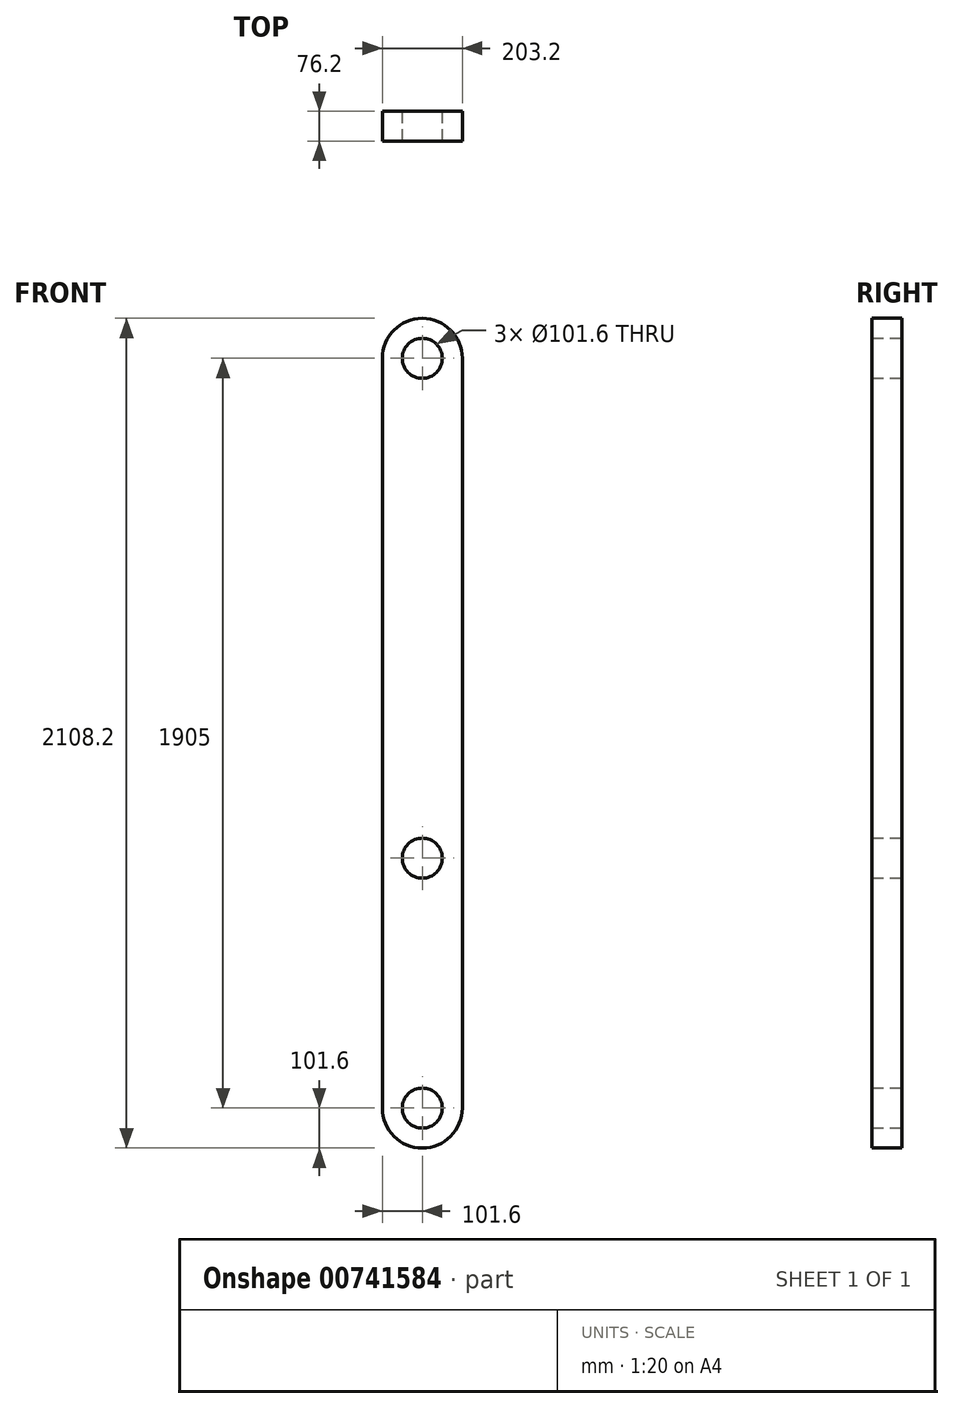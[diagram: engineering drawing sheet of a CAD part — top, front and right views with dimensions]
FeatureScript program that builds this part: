
annotation { "Feature Type Name" : "Feature", "Feature Type Description" : "" }
export const myFeature = defineFeature(function(context is Context, id is Id, definition is map)
    precondition{}
    {
        {
            var Q0;
            Q0=qCreatedBy(makeId("Front.planeOp"),FACE);
            var sketch = newSketch(context, id + "F0", { "sketchPlane" : qUnion([Q0])});
            skLineSegment(sketch, "E0.bottom", {"start": v(101.6, 0) * mm, "end": v(101.6, 0) * mm});
            skLineSegment(sketch, "E0.top", {"start": v(101.6, 2108.2) * mm, "end": v(101.6, 2108.2) * mm});
            skLineSegment(sketch, "E0.left", {"start": v(0, 101.6) * mm, "end": v(0, 2006.6) * mm});
            skLineSegment(sketch, "E0.right", {"start": v(203.2, 101.6) * mm, "end": v(203.2, 2006.6) * mm});
            skPoint(sketch, "E1.visualSharp", {"position": v(0, 2108.2) * mm});
            skArc(sketch, "E1.filletArc", {"start": v(101.6, 2108.2) * mm, "mid": v(29.76, 2078.44) * mm, "end": v(0, 2006.6) * mm});
            skPoint(sketch, "E2.visualSharp", {"position": v(0, 0) * mm});
            skArc(sketch, "E2.filletArc", {"start": v(0, 101.6) * mm, "mid": v(29.76, 29.76) * mm, "end": v(101.6, 0) * mm});
            skPoint(sketch, "E3.visualSharp", {"position": v(203.2, 0) * mm});
            skArc(sketch, "E3.filletArc", {"start": v(101.6, 0) * mm, "mid": v(173.44, 29.76) * mm, "end": v(203.2, 101.6) * mm});
            skPoint(sketch, "E4.visualSharp", {"position": v(203.2, 2108.2) * mm});
            skArc(sketch, "E4.filletArc", {"start": v(203.2, 2006.6) * mm, "mid": v(173.44, 2078.44) * mm, "end": v(101.6, 2108.2) * mm});
            skCircle(sketch, "E5", {"center": v(101.6, 2006.6) * mm, "radius": 50.8 * mm});
            skCircle(sketch, "E6", {"center": v(101.6, 101.6) * mm, "radius": 50.8 * mm});
            skCircle(sketch, "E7", {"center": v(101.6, 736.6) * mm, "radius": 50.8 * mm});
            skSolve(sketch);
        }
        {
            var Q0;
            Q0=makeQuery(id+"F0.imprint","IMPRINT",FACE,{"disambiguationData":[TD([[makeQuery(id+"F0.imprint","IMPRINT",EDGE,{"derivedFrom":sQuery(id+"F0.wireOp",EDGE,"E0.left")}),-1.0]])]});
            extrude(context, id + "F1", {"entities" : qUnion([Q0]), "depth" : 76.2 * mm, "offsetDistance" : 25.4 * mm});
        }
    });
